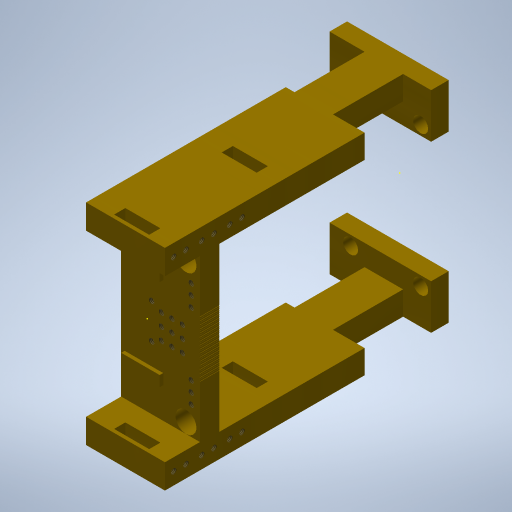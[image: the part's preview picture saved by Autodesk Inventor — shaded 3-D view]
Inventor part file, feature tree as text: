
AUTODESK INVENTOR PART (.ipt)
format: ipt  version: 2024 (Build 280153000, 153)  size: 835,584 bytes
history: native  units: mm
features: extrude x18, sketch x6, hole x5, pattern_linear x1
ambient origin geometry x8: Origin, YZ Plane, XZ Plane, XY Plane, X Axis, Y Axis, Z Axis, Center Point
bodies: Solid1 (feature_tree)
feature tree (30):
  extrude  "Extrusion1"  Depth=30.0mm
  extrude  "Extrusion2"  Depth=30.0mm
  extrude  "Extrusion3"  Depth=66.5mm TaperAngle=0.0deg
  pattern_linear  "Rectangular Pattern1"  Count1=2  [1 undecoded]
  hole  "Hole2"  [1 undecoded]
  extrude  "Extrusion6"  Depth=20.0mm
  hole  "Hole4"  [1 undecoded]
  extrude  "Extrusion7"  Depth=20.0mm
  extrude  "Extrusion8"  Depth=5.0mm
  extrude  "Extrusion9"  Depth=1.0mm TaperAngle=0.0deg
  extrude  "Extrusion10"  Depth=60.0mm TaperAngle=0.0deg
  extrude  "Extrusion13"  Depth=5.0mm
  extrude  "Extrusion14"  Depth=20.0mm
  extrude  "Extrusion15"  TaperAngle=0.0deg  [1 undecoded]
  extrude  "Extrusion16"  Depth=5.0mm
  extrude  "Extrusion17"  Depth=20.0mm
  extrude  "Extrusion19"  Depth=8.0mm
  extrude  "Extrusion20"  Depth=8.0mm
  hole  "Hole8"  [1 undecoded]
  extrude  "Extrusion21"  TaperAngle=0.0deg  [1 undecoded]
  extrude  "Extrusion22"  TaperAngle=0.0deg  [1 undecoded]
  extrude  "Extrusion23"  Depth=6.0mm
  hole  "Hole9"  [1 undecoded]
  hole  "Hole10"  [1 undecoded]
  sketch  "Sketch12"  dims[d0=15.0mm d1=30.0mm]
  sketch  "Sketch15"  dims[d2=60.0mm d3=30.0mm]
  sketch  "Sketch26"  dims[d4=72.0mm d5=0.0mm d10=66.5mm d11=0.0mm d15=20.0mm]
  sketch  "Sketch28"  dims[d16=11.0mm d17=4.3mm]
  sketch  "Sketch29"  dims[d18=50.0mm d19=0.0mm d20=20.0mm d22=20.0mm]
  sketch  "Sketch36"  dims[d23=20.0mm d25=40.0mm d47=13.8mm d49=20.0mm d51=10.0mm d52=10.0mm d54=10.0mm d56=1.567mm d57=4.0mm d58=3.023mm d59=2.0mm d60=14.3117mm d61=6.3mm d62=0.0mm d85=5.0mm d91=1.0mm d92=0.0mm d104=0.2mm d105=6.0mm d106=4.0mm d107=2.0mm d108=90.0deg d109=8.0mm d110=20.594885mm d111=60.0mm d112=0.0mm d113=5.0mm d114=20.0mm d115=0.0mm d116=5.0mm d117=20.0mm d118=8.0mm d119=8.0mm d120=2.0mm d121=0.0mm d122=0.0mm d123=6.0mm d124=0.0mm d125=0.0mm d126=6.0mm d127=0.0mm d128=8.0mm d129=6.0mm d134=6.0mm d137=6.0mm d138=10.0mm d139=0.0mm d141=7.0mm d142=29.0mm d144=29.0mm d145=10.0mm d146=0.0mm d210=7.0mm d212=7.5mm d213=0.0mm d214=0.0mm d215=0.0mm d216=0.0mm d217=0.0mm d218=1.0mm d219=0.0mm d220=0.0mm d221=0.0mm d222=3.2mm d223=5.5mm d224=10.0mm d225=1.0mm d226=1.567mm d227=4.0mm d228=4.0mm d229=2.0mm d230=90.0deg d231=5.0mm d232=20.594885mm d235=3.5mm d236=3.5mm d237=2.5mm d238=3.5mm d239=3.5mm d240=3.5mm d241=2.5mm d242=10.0mm d243=3.2mm d244=27.5mm d245=0.25mm d246=0.0mm d249=0.5mm d250=0.0mm d251=1.0mm d252=0.0mm d253=3.5mm d254=4.5mm d255=3.5mm d256=4.5mm d257=3.5mm d258=3.5mm d259=4.5mm d260=4.5mm d261=15.0mm d262=0.0mm d263=1.5mm d264=7.0mm d265=7.0mm d266=8.0mm d267=8.0mm d268=3.2mm d270=3.2mm d272=4.0mm d273=4.0mm d274=10.0mm d275=0.0mm d276=2.0mm d277=2.0mm d278=2.0mm d279=2.0mm d280=3.0mm d281=11.0mm d282=1.0mm d283=1.0mm d284=3.0mm d285=11.0mm d286=1.0mm d287=0.0mm d292=1.0mm d293=1.0mm d294=1.0mm d295=1.0mm d296=1.0mm d297=0.1mm d298=6.0mm d299=4.0mm d300=2.0mm d301=90.0deg d302=8.0mm d303=20.594885mm d304=3.0mm d305=3.0mm d306=2.5mm d307=2.5mm d308=2.5mm d309=2.5mm d310=2.5mm d311=2.5mm d312=3.0mm d313=3.0mm d320=5.0mm d321=30.0mm d323=3.5mm d324=10.0mm d326=10.0mm d328=26.5mm d329=1.567mm d330=4.0mm d331=4.0mm d332=2.0mm d333=90.0deg d334=8.0mm d335=20.594885mm d336=30.0mm d338=3.0mm d339=10.0mm d341=10.0mm d343=15.0mm d344=15.0mm]
note: 9 required parameter values undecoded (feature->parameter linkage not recoverable at this tier; creation-order binding heuristic only, values carry confidence <= 0.55)
